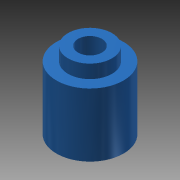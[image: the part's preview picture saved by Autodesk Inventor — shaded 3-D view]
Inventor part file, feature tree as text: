
AUTODESK INVENTOR PART (.ipt)
format: ipt  version: 2013 SP2 (Build 170200200, 200)  size: 89,600 bytes
history: native  units: mm
features: extrude x2, sketch x2
ambient origin geometry x8: Origin, YZ Plane, XZ Plane, XY Plane, X Axis, Y Axis, Z Axis, Center Point
bodies: Solid1 (feature_tree)
feature tree (4):
  extrude  "Extrusion1"  Depth=9.0mm
  extrude  "Extrusion2"  Depth=5.9mm
  sketch  "Sketch1"  dims[d0=3.2mm d1=9.0mm]
  sketch  "Sketch2"  dims[d2=8.5mm d3=0.0mm d4=5.9mm d5=1.8mm d6=0.0mm]
